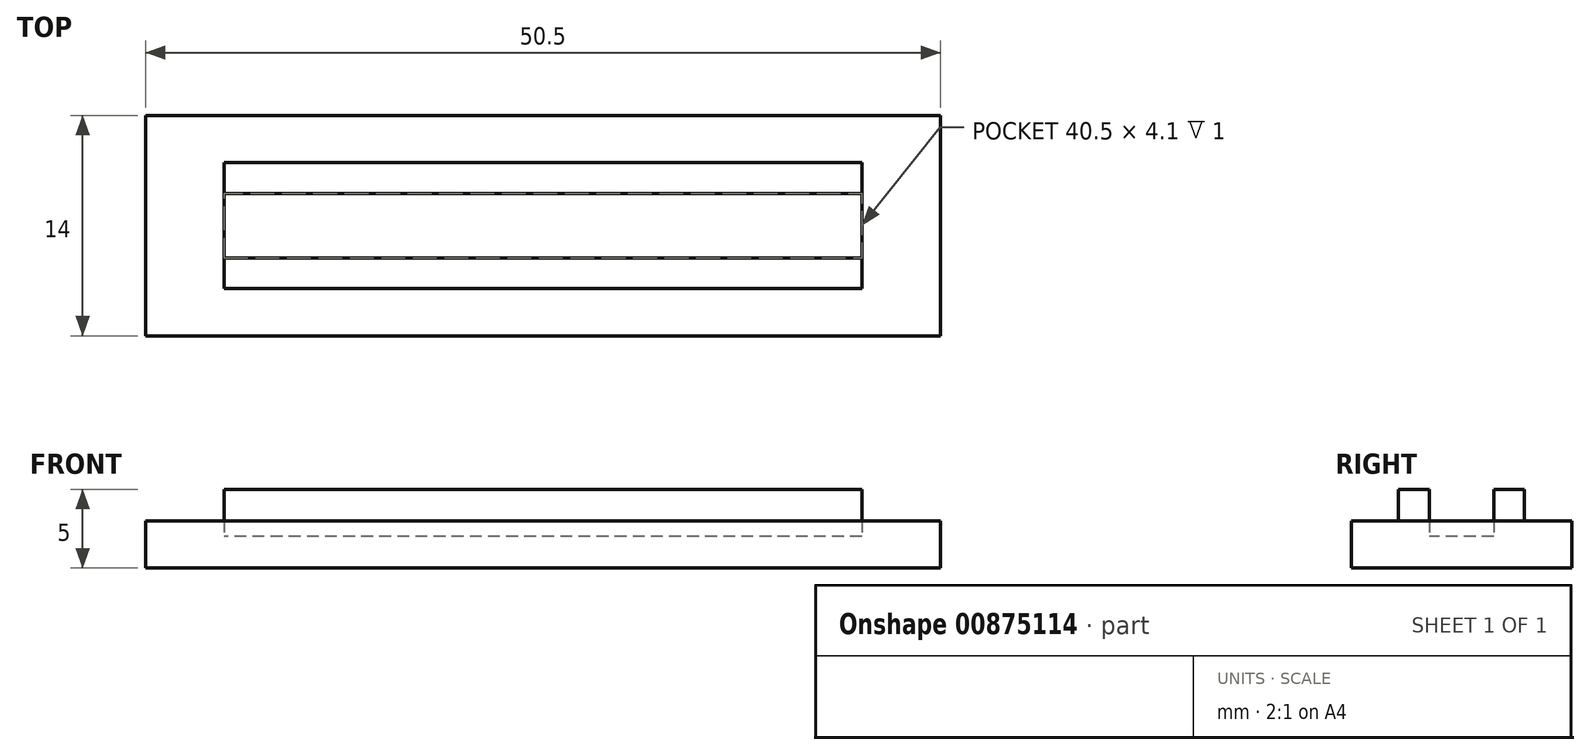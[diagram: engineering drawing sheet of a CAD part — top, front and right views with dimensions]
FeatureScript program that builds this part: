
annotation { "Feature Type Name" : "Feature", "Feature Type Description" : "" }
export const myFeature = defineFeature(function(context is Context, id is Id, definition is map)
    precondition{}
    {
        {
            var Q0;
            Q0=qCreatedBy(makeId("Top.planeOp"),FACE);
            var sketch = newSketch(context, id + "F0", { "sketchPlane" : qUnion([Q0])});
            skLineSegment(sketch, "E0.bottom", {"start": v(-25.25, -7) * mm, "end": v(25.25, -7) * mm});
            skLineSegment(sketch, "E0.top", {"start": v(-25.25, 7) * mm, "end": v(25.25, 7) * mm});
            skLineSegment(sketch, "E0.left", {"start": v(-25.25, -7) * mm, "end": v(-25.25, 7) * mm});
            skLineSegment(sketch, "E0.right", {"start": v(25.25, -7) * mm, "end": v(25.25, 7) * mm});
            skPoint(sketch, "E0.middle", {"position": v(0, 0) * mm});
            skLineSegment(sketch, "E1.bottom", {"start": v(-20.25, 4) * mm, "end": v(20.25, 4) * mm});
            skLineSegment(sketch, "E1.top", {"start": v(-20.25, -4) * mm, "end": v(20.25, -4) * mm});
            skLineSegment(sketch, "E1.left", {"start": v(-20.25, 4) * mm, "end": v(-20.25, -4) * mm});
            skLineSegment(sketch, "E1.right", {"start": v(20.25, 4) * mm, "end": v(20.25, -4) * mm});
            skLineSegment(sketch, "E2.top", {"start": v(-20.25, -2.05) * mm, "end": v(20.25, -2.05) * mm});
            skLineSegment(sketch, "E2.left", {"start": v(-20.25, -4) * mm, "end": v(-20.25, -2.05) * mm});
            skLineSegment(sketch, "E2.right", {"start": v(20.25, -4) * mm, "end": v(20.25, -2.05) * mm});
            skLineSegment(sketch, "E3.top", {"start": v(-20.25, 2.05) * mm, "end": v(20.25, 2.05) * mm});
            skLineSegment(sketch, "E3.left", {"start": v(-20.25, 4) * mm, "end": v(-20.25, 2.05) * mm});
            skLineSegment(sketch, "E3.right", {"start": v(20.25, 4) * mm, "end": v(20.25, 2.05) * mm});
            skSolve(sketch);
        }
        {
            var Q0;
            Q0=makeQuery(id+"F0.imprint","IMPRINT",FACE,{"disambiguationData":[TD([[makeQuery(id+"F0.imprint","IMPRINT",EDGE,{"derivedFrom":sQuery(id+"F0.wireOp",EDGE,"E1.left")}),1.0]])]});
            extrude(context, id + "F1", {"entities" : qUnion([Q0]), "depth" : 2 * mm, "offsetDistance" : 25 * mm});
        }
        {
            var Q0;
            Q0=makeQuery(id+"F0.imprint","IMPRINT",FACE,{"disambiguationData":[TD([[makeQuery(id+"F0.imprint","IMPRINT",EDGE,{"derivedFrom":sQuery(id+"F0.wireOp",EDGE,"E1.bottom")}),-1.0]])]});
            var Q1;
            Q1=makeQuery(id+"F0.imprint","IMPRINT",FACE,{"disambiguationData":[TD([[makeQuery(id+"F0.imprint","IMPRINT",EDGE,{"derivedFrom":sQuery(id+"F0.wireOp",EDGE,"E1.top")}),1.0]])]});
            extrude(context, id + "F2", {"entities" : qUnion([Q0, Q1]), "operationType" : NewBodyOperationType.ADD, "depth" : 5 * mm, "offsetDistance" : 25 * mm});
        }
        {
            var Q0;
            Q0=makeQuery(id+"F0.imprint","IMPRINT",FACE,{"disambiguationData":[TD([[makeQuery(id+"F0.imprint","IMPRINT",EDGE,{"derivedFrom":sQuery(id+"F0.wireOp",EDGE,"E0.bottom")}),1.0]])]});
            extrude(context, id + "F3", {"entities" : qUnion([Q0]), "operationType" : NewBodyOperationType.ADD, "depth" : 3 * mm, "offsetDistance" : 25 * mm});
        }
    });
